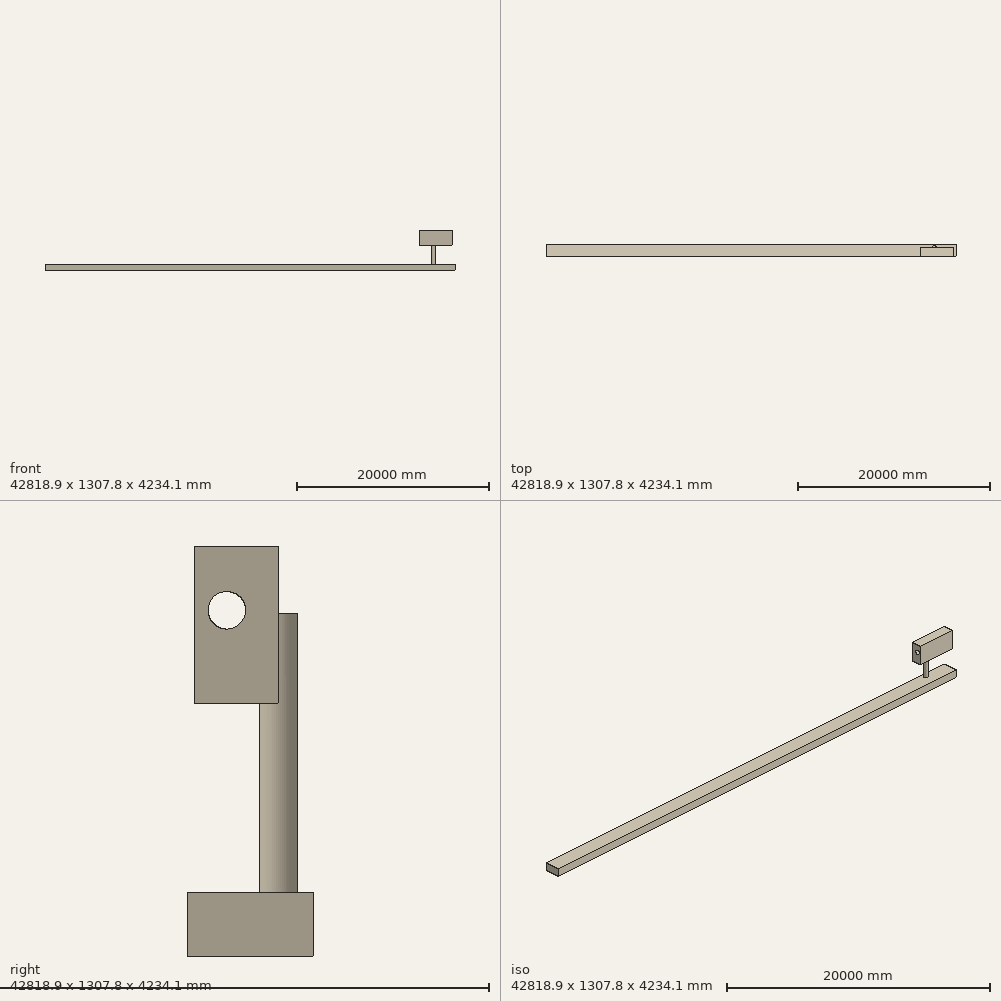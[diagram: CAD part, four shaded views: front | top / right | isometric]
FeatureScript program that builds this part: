
annotation { "Feature Type Name" : "Feature", "Feature Type Description" : "" }
export const myFeature = defineFeature(function(context is Context, id is Id, definition is map)
    precondition{}
    {
        {
            var Q0;
            Q0=qCreatedBy(makeId("Top.planeOp"),FACE);
            var sketch = newSketch(context, id + "F0", { "sketchPlane" : qUnion([Q0])});
            skCircle(sketch, "E0", {"center": v(0, 0) * mm, "radius": 200 * mm});
            skSolve(sketch);
        }
        {
            var Q0;
            Q0=makeQuery(id+"F0.imprint","IMPRINT",FACE,{"disambiguationData":[TD([[makeQuery(id+"F0.imprint","IMPRINT",EDGE,{"derivedFrom":sQuery(id+"F0.wireOp",EDGE,"E0")}),1.0]])]});
            extrude(context, id + "F1", {"entities" : qUnion([Q0]), "depth" : 2880 * mm, "offsetDistance" : 25 * mm});
        }
        {
            var Q0;
            Q0=qCreatedBy(makeId("Front.planeOp"),FACE);
            var sketch = newSketch(context, id + "F2", { "sketchPlane" : qUnion([Q0])});
            skLineSegment(sketch, "E1.bottom", {"start": v(-1453.42, 3574.13) * mm, "end": v(1956.74, 3574.13) * mm});
            skLineSegment(sketch, "E1.top", {"start": v(-1453.42, 1957.55) * mm, "end": v(1956.74, 1957.55) * mm});
            skLineSegment(sketch, "E1.left", {"start": v(-1453.42, 3574.13) * mm, "end": v(-1453.42, 1957.55) * mm});
            skLineSegment(sketch, "E1.right", {"start": v(1956.74, 3574.13) * mm, "end": v(1956.74, 1957.55) * mm});
            skSolve(sketch);
        }
        {
            var Q0;
            Q0=makeQuery(id+"F2.imprint","IMPRINT",FACE,{"disambiguationData":[TD([[makeQuery(id+"F2.imprint","IMPRINT",EDGE,{"derivedFrom":sQuery(id+"F2.wireOp",EDGE,"E1.bottom")}),-1.0]])]});
            extrude(context, id + "F3", {"entities" : qUnion([Q0]), "operationType" : NewBodyOperationType.ADD, "depth" : 870 * mm, "offsetDistance" : 25 * mm});
        }
        {
            var Q0;
            Q0=makeQuery(id+"F1.opExtrude","CAP_FACE",FACE,{"disambiguationData":[OSD([sQuery(id+"F0.wireOp",EDGE,"E0")])],"isStart":true});
            var sketch = newSketch(context, id + "F4", { "sketchPlane" : qUnion([Q0])});
            skLineSegment(sketch, "E2.bottom", {"start": v(2320.79, -364.1) * mm, "end": v(-40498.1, -364.1) * mm});
            skLineSegment(sketch, "E2.top", {"start": v(2320.79, 943.72) * mm, "end": v(-40498.1, 943.72) * mm});
            skLineSegment(sketch, "E2.left", {"start": v(2320.79, -364.1) * mm, "end": v(2320.79, 943.72) * mm});
            skLineSegment(sketch, "E2.right", {"start": v(-40498.1, -364.1) * mm, "end": v(-40498.1, 943.72) * mm});
            skSolve(sketch);
        }
        {
            var Q0;
            Q0 = qSketchRegion(id + "F4", true);
            extrude(context, id + "F5", {"entities" : qUnion([Q0]), "operationType" : NewBodyOperationType.ADD, "depth" : 660 * mm, "offsetDistance" : 25 * mm});
        }
        {
            var Q0;
            Q0=makeQuery(id+"F3.opExtrude","SWEPT_FACE",FACE,{"disambiguationData":[OSD([sQuery(id+"F2.wireOp",EDGE,"E1.right")])]});
            var sketch = newSketch(context, id + "F6", { "sketchPlane" : qUnion([Q0])});
            skCircle(sketch, "E3", {"center": v(-533.07, 2914.94) * mm, "radius": 193.5 * mm});
            skSolve(sketch);
        }
        {
            var Q0;
            Q0=makeQuery(id+"F6.imprint","IMPRINT",FACE,{"disambiguationData":[TD([[makeQuery(id+"F6.imprint","IMPRINT",EDGE,{"derivedFrom":sQuery(id+"F6.wireOp",EDGE,"E3")}),1.0]])]});
            extrude(context, id + "F7", {"entities" : qUnion([Q0]), "operationType" : NewBodyOperationType.REMOVE, "oppositeDirection" : true, "depth" : 5220 * mm, "offsetDistance" : 25 * mm});
        }
    });
